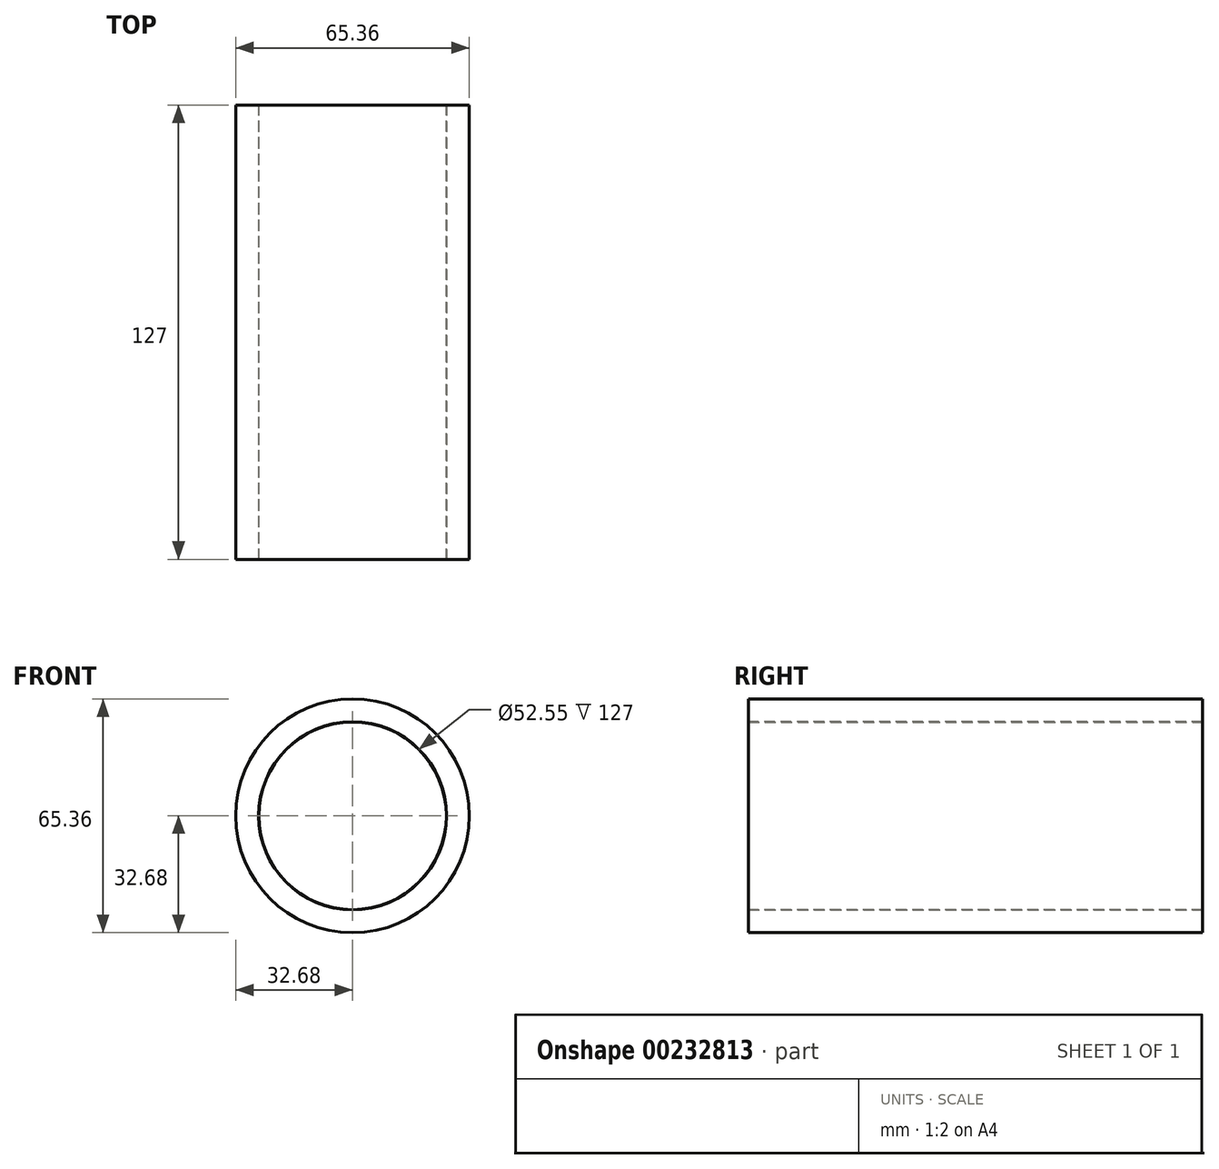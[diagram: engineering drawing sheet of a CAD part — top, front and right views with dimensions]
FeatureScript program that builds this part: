
annotation { "Feature Type Name" : "Feature", "Feature Type Description" : "" }
export const myFeature = defineFeature(function(context is Context, id is Id, definition is map)
    precondition{}
    {
        {
            var Q0;
            Q0=qCreatedBy(makeId("Front.planeOp"),FACE);
            var sketch = newSketch(context, id + "F0", { "sketchPlane" : qUnion([Q0])});
            skCircle(sketch, "E0", {"center": v(0, 0) * mm, "radius": 32.68 * mm});
            skSolve(sketch);
        }
        {
            var Q0;
            Q0 = qSketchRegion(id + "F0", true);
            extrude(context, id + "F1", {"entities" : qUnion([Q0]), "endBound" : BoundingType.SYMMETRIC, "depth" : 127 * mm});
        }
        {
            var Q0;
            Q0=qCreatedBy(makeId("Front.planeOp"),FACE);
            var sketch = newSketch(context, id + "F2", { "sketchPlane" : qUnion([Q0])});
            skCircle(sketch, "E1", {"center": v(0, 0) * mm, "radius": 26.27 * mm});
            skSolve(sketch);
        }
        {
            var Q0;
            Q0 = qSketchRegion(id + "F2", true);
            extrude(context, id + "F3", {"entities" : qUnion([Q0]), "operationType" : NewBodyOperationType.REMOVE, "endBound" : BoundingType.SYMMETRIC, "oppositeDirection" : true, "depth" : 254 * mm});
        }
        {
            var Q0;
            Q0=qCreatedBy(makeId("Front.planeOp"),FACE);
            var sketch = newSketch(context, id + "F4", { "sketchPlane" : qUnion([Q0])});
            skCircle(sketch, "E2", {"center": v(0, 0) * mm, "radius": 26.23 * mm});
            skSolve(sketch);
        }
        {
            var Q0;
            Q0 = qSketchRegion(id + "F4", true);
            extrude(context, id + "F5", {"entities" : qUnion([Q0]), "operationType" : NewBodyOperationType.ADD, "endBound" : BoundingType.SYMMETRIC, "depth" : 127 * mm});
        }
    });
